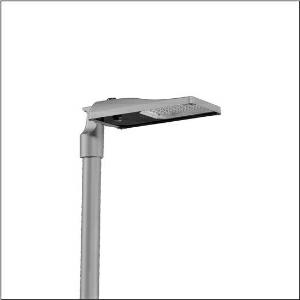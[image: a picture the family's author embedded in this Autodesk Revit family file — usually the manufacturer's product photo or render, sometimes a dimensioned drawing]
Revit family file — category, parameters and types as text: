
# Revit family: streetlight_sl_31_mini___st1_5a_5xh6p31t08ha_0610
name_source: partatom
category: Lighting Fixtures
units: mm (PartAtom-declared; Revit-internal decimal feet)

## family parameters
Cut with Voids When Loaded = No
Host = Face
Light Source = No
Part Type = Normal
Room Calculation Point = No
Round Connector Dimension = Use Diameter
Shared = No

## types (1)
- --- (1 x LED, 9070 lm, 68.3 W, 3000K)
    Apparent Load = 68 VA
    CIE Flux Codes = 22 53 95 100 100
    Color Rendering = 70
    Color Temperature = 3000K
    Default Elevation = 1800 mm
    Description = Streetlight SL 31 mini D4i, Desk-Remote mast luminaire for post-top, side-entry; light control with lens of PMMA; light distribution: ST1.5a, direct asymmetric distribution, for standard-compliant lighting for roads and squares; LED: luminous flux: 9.070lm, light colour: 730, colour temperature: 3000K; luminous efficacy: 132,8lm/W; control: pre-setting: logarithmic dimming characteristic, flexible luminous flux parameterisation, time-dependent luminous flux control, constant luminous flux control, power reduction, intelligent temperature release in ECG and LED module, overheat protection; luminaire housing, of diecast aluminium, SITECO metallic grey (DB 702S), corrosivity category C5 high according to DIN EN ISO 12944; cover of toughened safety glass, transparent, opened without tools; mast flange of diecast aluminium, SITECO metallic grey (DB 702S), spigot size: 76/60mm, mast flange included unmounted; cable length: 8,5m, connection cable pre-assembled; mains connection: 220..240V, AC, 50/60Hz; power consumption (at start of service life): 68,3W / (at end of service life): 74,5W / (with reduced operation 50%): 29,5W; protection rating (complete): IP66; insulation class (complete): insulation class II (safety insulation); impact resistance: IK09; certification: CE, ENEC, ENEC+, VDE, UKCA, ZD4i; permissible operating ambient temperature for outdoor applications: -40..+50°C; packaging unit: 1 piece

Light Distribution: ST1.5a
    Height = 76 mm
    Lamp = 1 x LED
    Lamp Light Flux = 9070 lm
    Lamp Power = 68.3 W
    Lamp count = 1
    Length = 547 mm
    Luminous efficacy = 133 lm/W
    Manufacturer = Siteco
    ModVariant = No
    Model = 5XH6P31T08HA
    Number of Poles = 1
    OnlyDefault = Yes
    Power Factor = 1
    Product Name = Streetlight SL 31 mini | ST1.5a
    Product group = mast luminaire | pylon top
    ProductGroupID = 6100
    Protection Class = Protection class II
    Protection Degree = IP 66
    RLX_Detail_Level = 1
    RLX_Emergency_Light_Flux = 0 lm
    RLX_Emergency_Type = 0
    RLX_Emergency_Type_DB = No
    RlxData = <blob elided: 27845 chars, md5=a796a099>
    Socket = socket
    Standby Power = 0 W
    System Light Flux = 9070 lm
    System Power = 68 W
    Type Comments = factory setting: luminous flux: 100 % | dim-lin: 254 | 692 mA
    Type Image = l_1300332.jpg
    URL = http://relux.com
    VarID = @adj_021713
    Voltage = 0 V
    Weight = 0.00 kg
    Width = 265 mm

## geometry (parser evidence)
native form markers: Blend x4, Sweep x11
no freeform markers — native parametric forms only
